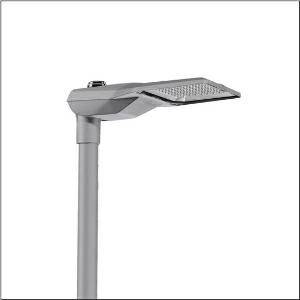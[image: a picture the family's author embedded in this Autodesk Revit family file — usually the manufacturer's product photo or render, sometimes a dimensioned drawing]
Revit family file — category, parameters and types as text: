
# Revit family: streetlight_sl_21_midi___stw1_0a_5xe7e47n08mb_f37a
name_source: partatom
category: Lighting Fixtures
units: mm (PartAtom-declared; Revit-internal decimal feet)

## family parameters
Cut with Voids When Loaded = No
Host = Face
Light Source = No
Part Type = Normal
Room Calculation Point = No
Round Connector Dimension = Use Diameter
Shared = No

## types (1)
- --- (1 x LED, 20180 lm, 147 W, 4000K)
    Apparent Load = 147 VA
    CIE Flux Codes = 38 75 98 100 100
    Color Rendering = 70
    Color Temperature = 4000K
    Default Elevation = 1800 mm
    Description = Streetlight SL 21 midi, mast luminaire, primary light control with lens, of PMMA, primary optical cover: cover, of toughened safety glass, transparent, light distribution: STW1.0a, light emission: direct distribution, primary light characteristic: asymmetric, installation type: side-entry, LED, 3G 2.5mm², High Power LED, rated luminous flux: 20.180lm, luminous efficacy: 137lm/W, light colour: 740, colour temperature: 4000K, control: overheat protection, pre-setting: linear dimming characteristic, constant luminous flux control, time-dependent luminous flux control, flexible luminous flux parameterisation, mains connection: 220..240V, AC, 50/60Hz, connection cable pre-assembled, cable length: 12,5m, wiring characteristics: H05VV-F, start of lifetime: 147W, end of service life: 155W, reduction: 65W, luminaire housing, of diecast aluminium (EN AC-44300), powder-coated, Siteco® metallic grey (DB 702S), corrosivity category C5 mid according to DIN EN ISO 12944, multi-level sealing system, sealing non-destructively replaceable, inclination adjustable: 0°, 5°, 10°, 15°, length: 644mm, width: 335mm, height: 110mm, spigot size: 42mm (side-entry), protection rating (complete): IP66, insulation class (complete): insulation class I (protective earthing), certification: CE, ENEC, ENEC+, VDE, impact resistance: IK09, permissible operating ambient temperature for outdoor applications: -40..+50°C, standard-compliant lighting for roads and squares, packaging unit: 1 piece

Light Distribution: STW1.0a
    Height = 111 mm
    Lamp = 1 x LED
    Lamp Light Flux = 20180 lm
    Lamp Power = 147 W
    Lamp count = 1
    Length = 644 mm
    Luminous efficacy = 137 lm/W
    Manufacturer = Siteco
    ModVariant = No
    Model = 5XE7E47N08MB
    Number of Poles = 1
    OnlyDefault = Yes
    Power Factor = 1
    Product Name = Streetlight SL 21 midi | STW1.0a
    Product group = mast luminaire | pylon top
    ProductGroupID = 6100
    Protection Class = Protection class I
    Protection Degree = IP 66
    RLX_Detail_Level = 1
    RLX_Emergency_Light_Flux = 0 lm
    RLX_Emergency_Type = 0
    RLX_Emergency_Type_DB = No
    RlxData = <blob elided: 90661 chars, md5=77ebd3e3>
    Socket = socket
    Standby Power = 0 W
    System Light Flux = 20180 lm
    System Power = 147 W
    Type Comments = factory setting: luminous flux: 100 % | dim-lin: 254 | 750 mA
    Type Image = l_1294377.jpg
    URL = http://relux.com
    VarID = @adj_105245
    Voltage = 0 V
    Weight = 0.00 kg
    Width = 336 mm

## geometry (parser evidence)
native form markers: Blend x4, Sweep x11
no freeform markers — native parametric forms only
